# Revit family: Bidet-Portable_Cleaner-KOHLER-K-28144K_1
name_source: partatom
category: Specialty Equipment
units: mm (PartAtom-declared; Revit-internal decimal feet)

## family parameters
Cut with Voids When Loaded = No
Host = Face
OmniClass Number = 23.31.23.00
OmniClass Title = Bidets
Part Type = Normal
Room Calculation Point = No
Round Connector Dimension = Use Diameter
Shared = No

## types (2) — shared parameters
ADA Compliant = No
Assembly Code = C1030200
Date Modified = 12/05/2022
Default Elevation = 36"
Description = Portable Bidet
Height = 6 1/4"
Length = 2"
Manufacturer = Kohler Co.
Master Format 2014 = 10 28 00
Master Format 2014 Name = Toilet, Bath, and Laundry Accessories
Material = Plastic
URL = https://www.kohlerasiapacific.com
WaterSense Certified = No
Width = 2 7/16"

## per-type parameters (varying)
| type | Finish | Model | Secondary Finish | Strap Finish | Type |
| WT-Pearl White | Kohler-Plastic-WT-Pearl_White | K-28144K-WT | Kohler-Plastic-95-Ice_Grey | Kohler-Plastic-95-Ice_Grey | 1 |
| HB1-Honed Black | Kohler-Plastic-HB1-Honed_Black | K-28144K-HB1 | Kohler-Plastic-HB1-Honed_Black | Kohler-Plastic-58-Thunder_Grey | 2 |

## geometry (parser evidence)
native form markers: Sweep x4
no freeform markers — native parametric forms only
